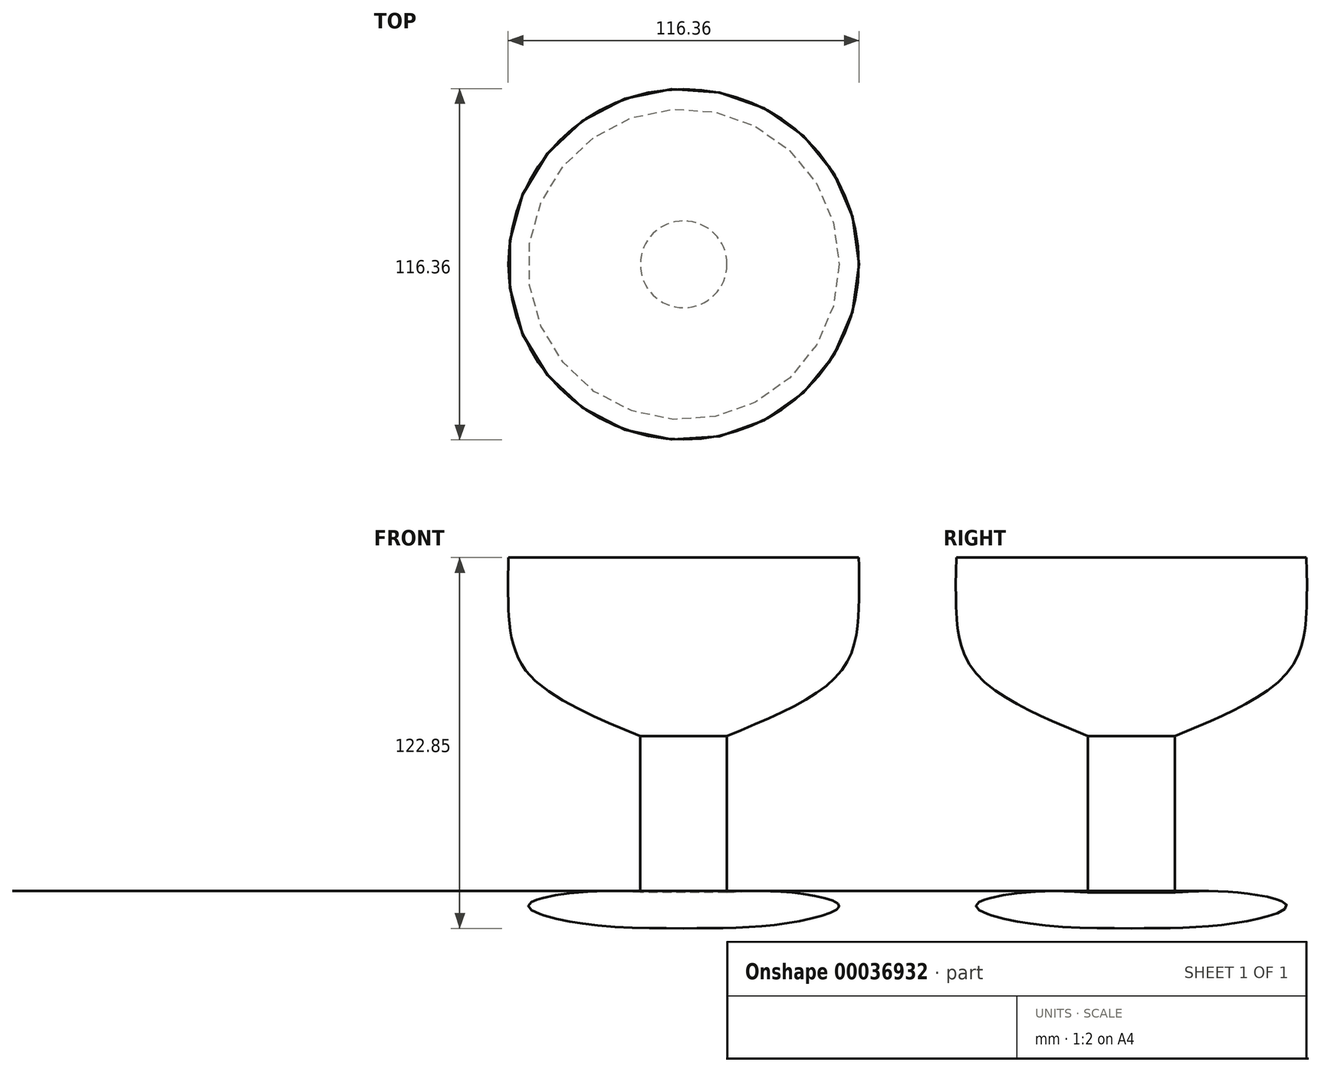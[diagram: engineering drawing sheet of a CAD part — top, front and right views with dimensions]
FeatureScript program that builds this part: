
annotation { "Feature Type Name" : "Feature", "Feature Type Description" : "" }
export const myFeature = defineFeature(function(context is Context, id is Id, definition is map)
    precondition{}
    {
        {
            var Q0;
            Q0=qCreatedBy(makeId("Front.planeOp"),FACE);
            var sketch = newSketch(context, id + "F0", { "sketchPlane" : qUnion([Q0])});
            skLineSegment(sketch, "E0", {"start": v(0, 52.66) * mm, "end": v(58.02, 52.66) * mm});
            skFitSpline(sketch, "E1", {"points": [v(58.02, 52.66) * mm, v(58.02, 35.3) * mm, v(52.06, 14.96) * mm, v(14.36, -6.46) * mm], "startDerivative": vector(1.48, -62.07) * mm, "endDerivative": vector(-107.43, -44.08) * mm});
            skLineSegment(sketch, "E2", {"start": v(14.36, -6.46) * mm, "end": v(14.36, -58.26) * mm});
            skFitSpline(sketch, "E3", {"points": [v(14.36, -58.26) * mm, v(34.97, -58.26) * mm, v(51.52, -62.6) * mm, v(37.14, -68.02) * mm, v(0, -70.2) * mm], "startDerivative": vector(77.56, 4.73) * mm, "endDerivative": vector(-116.65, -0.35) * mm});
            skLineSegment(sketch, "E4", {"start": v(0, 52.66) * mm, "end": v(0, -70.2) * mm});
            skSolve(sketch);
        }
        {
            var Q0;
            Q0=makeQuery(id+"F0.imprint","IMPRINT",FACE,{"disambiguationData":[TD([[makeQuery(id+"F0.imprint","IMPRINT",EDGE,{"derivedFrom":sQuery(id+"F0.wireOp",EDGE,"E0")}),-1.0]])]});
            var Q1;
            Q1=sQuery(id+"F0.wireOp",EDGE,"E4");
            revolve(context, id + "F1", {"entities" : qUnion([Q0]), "axis" : qUnion([Q1]), "revolveType" : RevolveType.FULL});
        }
    });
